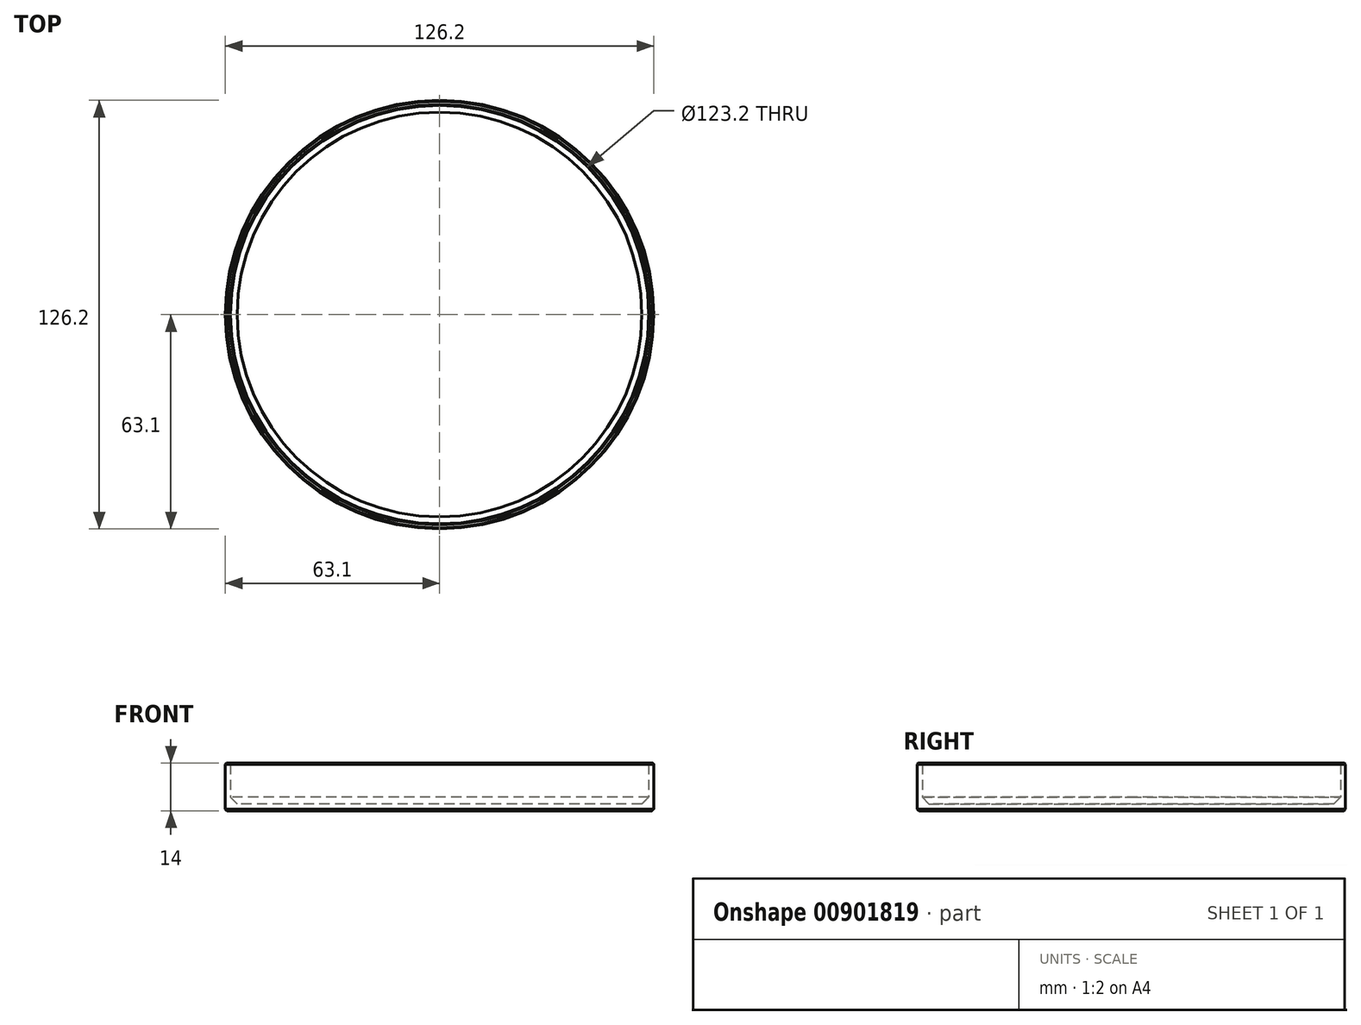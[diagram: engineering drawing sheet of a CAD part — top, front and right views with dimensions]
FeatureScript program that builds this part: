
annotation { "Feature Type Name" : "Feature", "Feature Type Description" : "" }
export const myFeature = defineFeature(function(context is Context, id is Id, definition is map)
    precondition{}
    {
        {
            var Q0;
            Q0=qCreatedBy(makeId("Top.planeOp"),FACE);
            var sketch = newSketch(context, id + "F0", { "sketchPlane" : qUnion([Q0])});
            skCircle(sketch, "E0", {"center": v(0, 0) * mm, "radius": 61.6 * mm});
            skCircle(sketch, "E1.0", {"center": v(0, 0) * mm, "radius": 63.1 * mm});
            skLineSegment(sketch, "E2", {"start": v(0, 0) * mm, "end": v(0, 61.6) * mm, "construction": true});
            skLineSegment(sketch, "E3", {"start": v(0, 61.6) * mm, "end": v(0, 63.1) * mm, "construction": true});
            skPoint(sketch, "E4", {"position": v(0, 62.2) * mm});
            skSolve(sketch);
        }
        {
            var Q0;
            Q0=makeQuery(id+"F0.imprint","IMPRINT",FACE,{"disambiguationData":[TD([[makeQuery(id+"F0.imprint","IMPRINT",EDGE,{"derivedFrom":sQuery(id+"F0.wireOp",EDGE,"E1.0")}),1.0]])]});
            var Q1;
            {var subQ1=sQuery(id+"F0.wireOp",EDGE,"E0");var subQ17=sQuery(id+"F0.wireOp",EDGE,"3fba6b06-569c-4ec6-a7ac-c338514c2173.7.0");var subQ18=makeQuery(id+"F0.imprint","INTERSECT",VERTEX,{"disambiguationData":[OD(0.0)],"derivedFrom":[subQ1,subQ17]});Q1=makeQuery(id+"F0.imprint","IMPRINT",FACE,{"disambiguationData":[TD([[makeQuery(id+"F0.imprint","IMPRINT",EDGE,{"disambiguationData":[TD([[subQ18,1.0]])],"derivedFrom":subQ1}),1.0]])]});}
            var Q2;
            {var subQ0=sQuery(id+"F0.wireOp",EDGE,"3fba6b06-569c-4ec6-a7ac-c338514c2173.4.0");var subQ1=sQuery(id+"F0.wireOp",EDGE,"E0");var subQ2=makeQuery(id+"F0.imprint","INTERSECT",VERTEX,{"disambiguationData":[OD(0.0)],"derivedFrom":[subQ1,subQ0]});Q2=makeQuery(id+"F0.imprint","IMPRINT",FACE,{"disambiguationData":[TD([[makeQuery(id+"F0.imprint","IMPRINT",EDGE,{"disambiguationData":[TD([[subQ2,-1.0]])],"derivedFrom":subQ1}),-1.0]])]});}
            var Q3;
            {var subQ0=sQuery(id+"F0.wireOp",EDGE,"3fba6b06-569c-4ec6-a7ac-c338514c2173.7.0");var subQ1=sQuery(id+"F0.wireOp",EDGE,"E0");var subQ2=makeQuery(id+"F0.imprint","INTERSECT",VERTEX,{"disambiguationData":[OD(0.0)],"derivedFrom":[subQ1,subQ0]});Q3=makeQuery(id+"F0.imprint","IMPRINT",FACE,{"disambiguationData":[TD([[makeQuery(id+"F0.imprint","IMPRINT",EDGE,{"disambiguationData":[TD([[subQ2,-1.0]])],"derivedFrom":subQ1}),-1.0]])]});}
            var Q4;
            {var subQ0=sQuery(id+"F0.wireOp",EDGE,"3fba6b06-569c-4ec6-a7ac-c338514c2173.1.0");var subQ1=sQuery(id+"F0.wireOp",EDGE,"E0");var subQ2=makeQuery(id+"F0.imprint","INTERSECT",VERTEX,{"disambiguationData":[OD(0.0)],"derivedFrom":[subQ1,subQ0]});Q4=makeQuery(id+"F0.imprint","IMPRINT",FACE,{"disambiguationData":[TD([[makeQuery(id+"F0.imprint","IMPRINT",EDGE,{"disambiguationData":[TD([[subQ2,-1.0]])],"derivedFrom":subQ1}),1.0]])]});}
            var Q5;
            {var subQ0=sQuery(id+"F0.wireOp",EDGE,"3fba6b06-569c-4ec6-a7ac-c338514c2173.2.0");var subQ1=sQuery(id+"F0.wireOp",EDGE,"E0");var subQ2=makeQuery(id+"F0.imprint","INTERSECT",VERTEX,{"disambiguationData":[OD(0.0)],"derivedFrom":[subQ1,subQ0]});Q5=makeQuery(id+"F0.imprint","IMPRINT",FACE,{"disambiguationData":[TD([[makeQuery(id+"F0.imprint","IMPRINT",EDGE,{"disambiguationData":[TD([[subQ2,-1.0]])],"derivedFrom":subQ1}),-1.0]])]});}
            var Q6;
            {var subQ0=sQuery(id+"F0.wireOp",EDGE,"3fba6b06-569c-4ec6-a7ac-c338514c2173.4.0");var subQ1=sQuery(id+"F0.wireOp",EDGE,"E0");var subQ2=makeQuery(id+"F0.imprint","INTERSECT",VERTEX,{"disambiguationData":[OD(0.0)],"derivedFrom":[subQ1,subQ0]});Q6=makeQuery(id+"F0.imprint","IMPRINT",FACE,{"disambiguationData":[TD([[makeQuery(id+"F0.imprint","IMPRINT",EDGE,{"disambiguationData":[TD([[subQ2,-1.0]])],"derivedFrom":subQ1}),1.0]])]});}
            var Q7;
            {var subQ0=sQuery(id+"F0.wireOp",EDGE,"3fba6b06-569c-4ec6-a7ac-c338514c2173.3.0");var subQ1=sQuery(id+"F0.wireOp",EDGE,"E0");var subQ2=makeQuery(id+"F0.imprint","INTERSECT",VERTEX,{"disambiguationData":[OD(0.0)],"derivedFrom":[subQ1,subQ0]});Q7=makeQuery(id+"F0.imprint","IMPRINT",FACE,{"disambiguationData":[TD([[makeQuery(id+"F0.imprint","IMPRINT",EDGE,{"disambiguationData":[TD([[subQ2,-1.0]])],"derivedFrom":subQ1}),-1.0]])]});}
            var Q8;
            {var subQ0=sQuery(id+"F0.wireOp",EDGE,"3fba6b06-569c-4ec6-a7ac-c338514c2173.5.0");var subQ1=sQuery(id+"F0.wireOp",EDGE,"E0");var subQ2=makeQuery(id+"F0.imprint","INTERSECT",VERTEX,{"disambiguationData":[OD(0.0)],"derivedFrom":[subQ1,subQ0]});Q8=makeQuery(id+"F0.imprint","IMPRINT",FACE,{"disambiguationData":[TD([[makeQuery(id+"F0.imprint","IMPRINT",EDGE,{"disambiguationData":[TD([[subQ2,-1.0]])],"derivedFrom":subQ1}),-1.0]])]});}
            var Q9;
            {var subQ0=sQuery(id+"F0.wireOp",EDGE,"3fba6b06-569c-4ec6-a7ac-c338514c2173.6.0");var subQ1=sQuery(id+"F0.wireOp",EDGE,"E0");var subQ2=makeQuery(id+"F0.imprint","INTERSECT",VERTEX,{"disambiguationData":[OD(0.0)],"derivedFrom":[subQ1,subQ0]});Q9=makeQuery(id+"F0.imprint","IMPRINT",FACE,{"disambiguationData":[TD([[makeQuery(id+"F0.imprint","IMPRINT",EDGE,{"disambiguationData":[TD([[subQ2,1.0]])],"derivedFrom":subQ1}),-1.0]])]});}
            var Q10;
            {var subQ0=sQuery(id+"F0.wireOp",EDGE,"3fba6b06-569c-4ec6-a7ac-c338514c2173.2.0");var subQ1=sQuery(id+"F0.wireOp",EDGE,"E0");var subQ2=makeQuery(id+"F0.imprint","INTERSECT",VERTEX,{"disambiguationData":[OD(0.0)],"derivedFrom":[subQ1,subQ0]});Q10=makeQuery(id+"F0.imprint","IMPRINT",FACE,{"disambiguationData":[TD([[makeQuery(id+"F0.imprint","IMPRINT",EDGE,{"disambiguationData":[TD([[subQ2,-1.0]])],"derivedFrom":subQ1}),1.0]])]});}
            var Q11;
            {var subQ0=sQuery(id+"F0.wireOp",EDGE,"3fba6b06-569c-4ec6-a7ac-c338514c2173.3.0");var subQ1=sQuery(id+"F0.wireOp",EDGE,"E0");var subQ2=makeQuery(id+"F0.imprint","INTERSECT",VERTEX,{"disambiguationData":[OD(0.0)],"derivedFrom":[subQ1,subQ0]});Q11=makeQuery(id+"F0.imprint","IMPRINT",FACE,{"disambiguationData":[TD([[makeQuery(id+"F0.imprint","IMPRINT",EDGE,{"disambiguationData":[TD([[subQ2,-1.0]])],"derivedFrom":subQ1}),1.0]])]});}
            var Q12;
            {var subQ0=sQuery(id+"F0.wireOp",EDGE,"3fba6b06-569c-4ec6-a7ac-c338514c2173.1.0");var subQ1=sQuery(id+"F0.wireOp",EDGE,"E0");var subQ2=makeQuery(id+"F0.imprint","INTERSECT",VERTEX,{"disambiguationData":[OD(0.0)],"derivedFrom":[subQ1,subQ0]});Q12=makeQuery(id+"F0.imprint","IMPRINT",FACE,{"disambiguationData":[TD([[makeQuery(id+"F0.imprint","IMPRINT",EDGE,{"disambiguationData":[TD([[subQ2,-1.0]])],"derivedFrom":subQ1}),-1.0]])]});}
            var Q13;
            {var subQ0=sQuery(id+"F0.wireOp",EDGE,"3fba6b06-569c-4ec6-a7ac-c338514c2173.7.0");var subQ1=sQuery(id+"F0.wireOp",EDGE,"E0");var subQ2=makeQuery(id+"F0.imprint","INTERSECT",VERTEX,{"disambiguationData":[OD(0.0)],"derivedFrom":[subQ1,subQ0]});Q13=makeQuery(id+"F0.imprint","IMPRINT",FACE,{"disambiguationData":[TD([[makeQuery(id+"F0.imprint","IMPRINT",EDGE,{"disambiguationData":[TD([[subQ2,-1.0]])],"derivedFrom":subQ1}),1.0]])]});}
            var Q14;
            {var subQ0=sQuery(id+"F0.wireOp",EDGE,"3fba6b06-569c-4ec6-a7ac-c338514c2173.5.0");var subQ1=sQuery(id+"F0.wireOp",EDGE,"E0");var subQ2=makeQuery(id+"F0.imprint","INTERSECT",VERTEX,{"disambiguationData":[OD(0.0)],"derivedFrom":[subQ1,subQ0]});Q14=makeQuery(id+"F0.imprint","IMPRINT",FACE,{"disambiguationData":[TD([[makeQuery(id+"F0.imprint","IMPRINT",EDGE,{"disambiguationData":[TD([[subQ2,-1.0]])],"derivedFrom":subQ1}),1.0]])]});}
            var Q15;
            {var subQ0=sQuery(id+"F0.wireOp",EDGE,"3fba6b06-569c-4ec6-a7ac-c338514c2173.6.0");var subQ1=sQuery(id+"F0.wireOp",EDGE,"E0");var subQ2=makeQuery(id+"F0.imprint","INTERSECT",VERTEX,{"disambiguationData":[OD(0.0)],"derivedFrom":[subQ1,subQ0]});Q15=makeQuery(id+"F0.imprint","IMPRINT",FACE,{"disambiguationData":[TD([[makeQuery(id+"F0.imprint","IMPRINT",EDGE,{"disambiguationData":[TD([[subQ2,1.0]])],"derivedFrom":subQ1}),1.0]])]});}
            var Q16;
            {var subQ0=sQuery(id+"F0.wireOp",EDGE,"yAiZnoHs-aMuX-z35t-Q1TA-KvtIRSM4lGY5");var subQ1=sQuery(id+"F0.wireOp",EDGE,"E0");var subQ2=makeQuery(id+"F0.imprint","INTERSECT",VERTEX,{"disambiguationData":[OD(0.0)],"derivedFrom":[subQ1,subQ0]});Q16=makeQuery(id+"F0.imprint","IMPRINT",FACE,{"disambiguationData":[TD([[makeQuery(id+"F0.imprint","IMPRINT",EDGE,{"disambiguationData":[TD([[subQ2,-1.0]])],"derivedFrom":subQ1}),1.0]])]});}
            var Q17;
            {var subQ0=sQuery(id+"F0.wireOp",EDGE,"yAiZnoHs-aMuX-z35t-Q1TA-KvtIRSM4lGY5");var subQ1=sQuery(id+"F0.wireOp",EDGE,"E0");var subQ2=makeQuery(id+"F0.imprint","INTERSECT",VERTEX,{"disambiguationData":[OD(0.0)],"derivedFrom":[subQ1,subQ0]});Q17=makeQuery(id+"F0.imprint","IMPRINT",FACE,{"disambiguationData":[TD([[makeQuery(id+"F0.imprint","IMPRINT",EDGE,{"disambiguationData":[TD([[subQ2,-1.0]])],"derivedFrom":subQ1}),-1.0]])]});}
            extrude(context, id + "F1", {"entities" : qUnion([Q0, Q1, Q2, Q3, Q4, Q5, Q6, Q7, Q8, Q9, Q10, Q11, Q12, Q13, Q14, Q15, Q16, Q17]), "depth" : 2 * mm, "offsetDistance" : 25 * mm});
        }
        {
            var Q0;
            Q0=makeQuery(id+"F0.imprint","IMPRINT",FACE,{"disambiguationData":[TD([[makeQuery(id+"F0.imprint","IMPRINT",EDGE,{"derivedFrom":sQuery(id+"F0.wireOp",EDGE,"E1.0")}),1.0]])]});
            extrude(context, id + "F2", {"entities" : qUnion([Q0]), "operationType" : NewBodyOperationType.ADD, "depth" : (1 + 13) * mm, "offsetDistance" : 25 * mm});
        }
        {
            var Q0;
            Q0=makeQuery(id+"F1.opExtrude","CAP_EDGE",EDGE,{"disambiguationData":[OSD([sQuery(id+"F0.wireOp",EDGE,"E1.0")])],"isStart":true});
            chamfer(context, id + "F3", {"entities" : qUnion([Q0]), "width" : 0.5 * mm, "tangentPropagation" : true});
        }
        {
            var Q0;
            {var subQ0=sQuery(id+"F0.wireOp",EDGE,"E0");Q0=makeQuery(id+"F2.boolean.opBoolean","INTERSECT",EDGE,{"derivedFrom":[makeQuery(id+"F1.opExtrude","CAP_FACE",FACE,{"disambiguationData":[OSD([sQuery(id+"F0.wireOp",EDGE,"E1.0")])],"isStart":false}),makeQuery(id+"F2.opExtrude","SWEPT_FACE",FACE,{"disambiguationData":[OSD([subQ0]),TDD([makeQuery(id+"F0.imprint","IMPRINT",EDGE,{"disambiguationData":[TD([[makeQuery(id+"F0.imprint","INTERSECT",VERTEX,{"disambiguationData":[OD(1.0)],"derivedFrom":[subQ0,sQuery(id+"F0.wireOp",EDGE,"yAiZnoHs-aMuX-z35t-Q1TA-KvtIRSM4lGY5")]}),-1.0]])],"derivedFrom":subQ0})])]})]});}
            var Q1;
            {var subQ0=sQuery(id+"F0.wireOp",EDGE,"E0");Q1=makeQuery(id+"F2.boolean.opBoolean","INTERSECT",EDGE,{"derivedFrom":[makeQuery(id+"F1.opExtrude","CAP_FACE",FACE,{"disambiguationData":[OSD([sQuery(id+"F0.wireOp",EDGE,"E1.0")])],"isStart":false}),makeQuery(id+"F2.opExtrude","SWEPT_FACE",FACE,{"disambiguationData":[OSD([subQ0]),TDD([makeQuery(id+"F0.imprint","IMPRINT",EDGE,{"disambiguationData":[TD([[makeQuery(id+"F0.imprint","INTERSECT",VERTEX,{"disambiguationData":[OD(1.0)],"derivedFrom":[subQ0,sQuery(id+"F0.wireOp",EDGE,"3fba6b06-569c-4ec6-a7ac-c338514c2173.7.0")]}),-1.0]])],"derivedFrom":subQ0})])]})]});}
            var Q2;
            {var subQ0=sQuery(id+"F0.wireOp",EDGE,"E0");Q2=makeQuery(id+"F2.boolean.opBoolean","INTERSECT",EDGE,{"derivedFrom":[makeQuery(id+"F1.opExtrude","CAP_FACE",FACE,{"disambiguationData":[OSD([sQuery(id+"F0.wireOp",EDGE,"E1.0")])],"isStart":false}),makeQuery(id+"F2.opExtrude","SWEPT_FACE",FACE,{"disambiguationData":[OSD([subQ0]),TDD([makeQuery(id+"F0.imprint","IMPRINT",EDGE,{"disambiguationData":[TD([[makeQuery(id+"F0.imprint","INTERSECT",VERTEX,{"disambiguationData":[OD(0.0)],"derivedFrom":[subQ0,sQuery(id+"F0.wireOp",EDGE,"3fba6b06-569c-4ec6-a7ac-c338514c2173.7.0")]}),1.0]])],"derivedFrom":subQ0})])]})]});}
            var Q3;
            {var subQ0=sQuery(id+"F0.wireOp",EDGE,"E0");Q3=makeQuery(id+"F2.boolean.opBoolean","INTERSECT",EDGE,{"derivedFrom":[makeQuery(id+"F1.opExtrude","CAP_FACE",FACE,{"disambiguationData":[OSD([sQuery(id+"F0.wireOp",EDGE,"E1.0")])],"isStart":false}),makeQuery(id+"F2.opExtrude","SWEPT_FACE",FACE,{"disambiguationData":[OSD([subQ0]),TDD([makeQuery(id+"F0.imprint","IMPRINT",EDGE,{"disambiguationData":[TD([[makeQuery(id+"F0.imprint","INTERSECT",VERTEX,{"disambiguationData":[OD(1.0)],"derivedFrom":[subQ0,sQuery(id+"F0.wireOp",EDGE,"3fba6b06-569c-4ec6-a7ac-c338514c2173.5.0")]}),-1.0]])],"derivedFrom":subQ0})])]})]});}
            var Q4;
            {var subQ0=sQuery(id+"F0.wireOp",EDGE,"E0");Q4=makeQuery(id+"F2.boolean.opBoolean","INTERSECT",EDGE,{"derivedFrom":[makeQuery(id+"F1.opExtrude","CAP_FACE",FACE,{"disambiguationData":[OSD([sQuery(id+"F0.wireOp",EDGE,"E1.0")])],"isStart":false}),makeQuery(id+"F2.opExtrude","SWEPT_FACE",FACE,{"disambiguationData":[OSD([subQ0]),TDD([makeQuery(id+"F0.imprint","IMPRINT",EDGE,{"disambiguationData":[TD([[makeQuery(id+"F0.imprint","INTERSECT",VERTEX,{"disambiguationData":[OD(1.0)],"derivedFrom":[subQ0,sQuery(id+"F0.wireOp",EDGE,"3fba6b06-569c-4ec6-a7ac-c338514c2173.4.0")]}),-1.0]])],"derivedFrom":subQ0})])]})]});}
            var Q5;
            {var subQ0=sQuery(id+"F0.wireOp",EDGE,"E0");Q5=makeQuery(id+"F2.boolean.opBoolean","INTERSECT",EDGE,{"derivedFrom":[makeQuery(id+"F1.opExtrude","CAP_FACE",FACE,{"disambiguationData":[OSD([sQuery(id+"F0.wireOp",EDGE,"E1.0")])],"isStart":false}),makeQuery(id+"F2.opExtrude","SWEPT_FACE",FACE,{"disambiguationData":[OSD([subQ0]),TDD([makeQuery(id+"F0.imprint","IMPRINT",EDGE,{"disambiguationData":[TD([[makeQuery(id+"F0.imprint","INTERSECT",VERTEX,{"disambiguationData":[OD(1.0)],"derivedFrom":[subQ0,sQuery(id+"F0.wireOp",EDGE,"3fba6b06-569c-4ec6-a7ac-c338514c2173.3.0")]}),-1.0]])],"derivedFrom":subQ0})])]})]});}
            var Q6;
            {var subQ0=sQuery(id+"F0.wireOp",EDGE,"E0");Q6=makeQuery(id+"F2.boolean.opBoolean","INTERSECT",EDGE,{"derivedFrom":[makeQuery(id+"F1.opExtrude","CAP_FACE",FACE,{"disambiguationData":[OSD([sQuery(id+"F0.wireOp",EDGE,"E1.0")])],"isStart":false}),makeQuery(id+"F2.opExtrude","SWEPT_FACE",FACE,{"disambiguationData":[OSD([subQ0]),TDD([makeQuery(id+"F0.imprint","IMPRINT",EDGE,{"disambiguationData":[TD([[makeQuery(id+"F0.imprint","INTERSECT",VERTEX,{"disambiguationData":[OD(1.0)],"derivedFrom":[subQ0,sQuery(id+"F0.wireOp",EDGE,"3fba6b06-569c-4ec6-a7ac-c338514c2173.2.0")]}),-1.0]])],"derivedFrom":subQ0})])]})]});}
            var Q7;
            {var subQ0=sQuery(id+"F0.wireOp",EDGE,"E0");Q7=makeQuery(id+"F2.boolean.opBoolean","INTERSECT",EDGE,{"derivedFrom":[makeQuery(id+"F1.opExtrude","CAP_FACE",FACE,{"disambiguationData":[OSD([sQuery(id+"F0.wireOp",EDGE,"E1.0")])],"isStart":false}),makeQuery(id+"F2.opExtrude","SWEPT_FACE",FACE,{"disambiguationData":[OSD([subQ0]),TDD([makeQuery(id+"F0.imprint","IMPRINT",EDGE,{"disambiguationData":[TD([[makeQuery(id+"F0.imprint","INTERSECT",VERTEX,{"disambiguationData":[OD(1.0)],"derivedFrom":[subQ0,sQuery(id+"F0.wireOp",EDGE,"3fba6b06-569c-4ec6-a7ac-c338514c2173.1.0")]}),-1.0]])],"derivedFrom":subQ0})])]})]});}
            chamfer(context, id + "F4", {"entities" : qUnion([Q0, Q1, Q2, Q3, Q4, Q5, Q6, Q7]), "width" : 2 * mm, "tangentPropagation" : true});
        }
        {
            var Q0;
            Q0=makeQuery(id+"F2.opExtrude","CAP_FACE",FACE,{"disambiguationData":[OSD([sQuery(id+"F0.wireOp",EDGE,"E0"),sQuery(id+"F0.wireOp",EDGE,"E1.0"),sQuery(id+"F0.wireOp",EDGE,"yAiZnoHs-aMuX-z35t-Q1TA-KvtIRSM4lGY5"),sQuery(id+"F0.wireOp",EDGE,"3fba6b06-569c-4ec6-a7ac-c338514c2173.1.0"),sQuery(id+"F0.wireOp",EDGE,"3fba6b06-569c-4ec6-a7ac-c338514c2173.2.0"),sQuery(id+"F0.wireOp",EDGE,"3fba6b06-569c-4ec6-a7ac-c338514c2173.3.0"),sQuery(id+"F0.wireOp",EDGE,"3fba6b06-569c-4ec6-a7ac-c338514c2173.4.0"),sQuery(id+"F0.wireOp",EDGE,"3fba6b06-569c-4ec6-a7ac-c338514c2173.5.0"),sQuery(id+"F0.wireOp",EDGE,"3fba6b06-569c-4ec6-a7ac-c338514c2173.6.0"),sQuery(id+"F0.wireOp",EDGE,"3fba6b06-569c-4ec6-a7ac-c338514c2173.7.0")])],"isStart":false});
            chamfer(context, id + "F5", {"entities" : qUnion([Q0]), "width" : 0.3 * mm, "tangentPropagation" : true});
        }
    });
